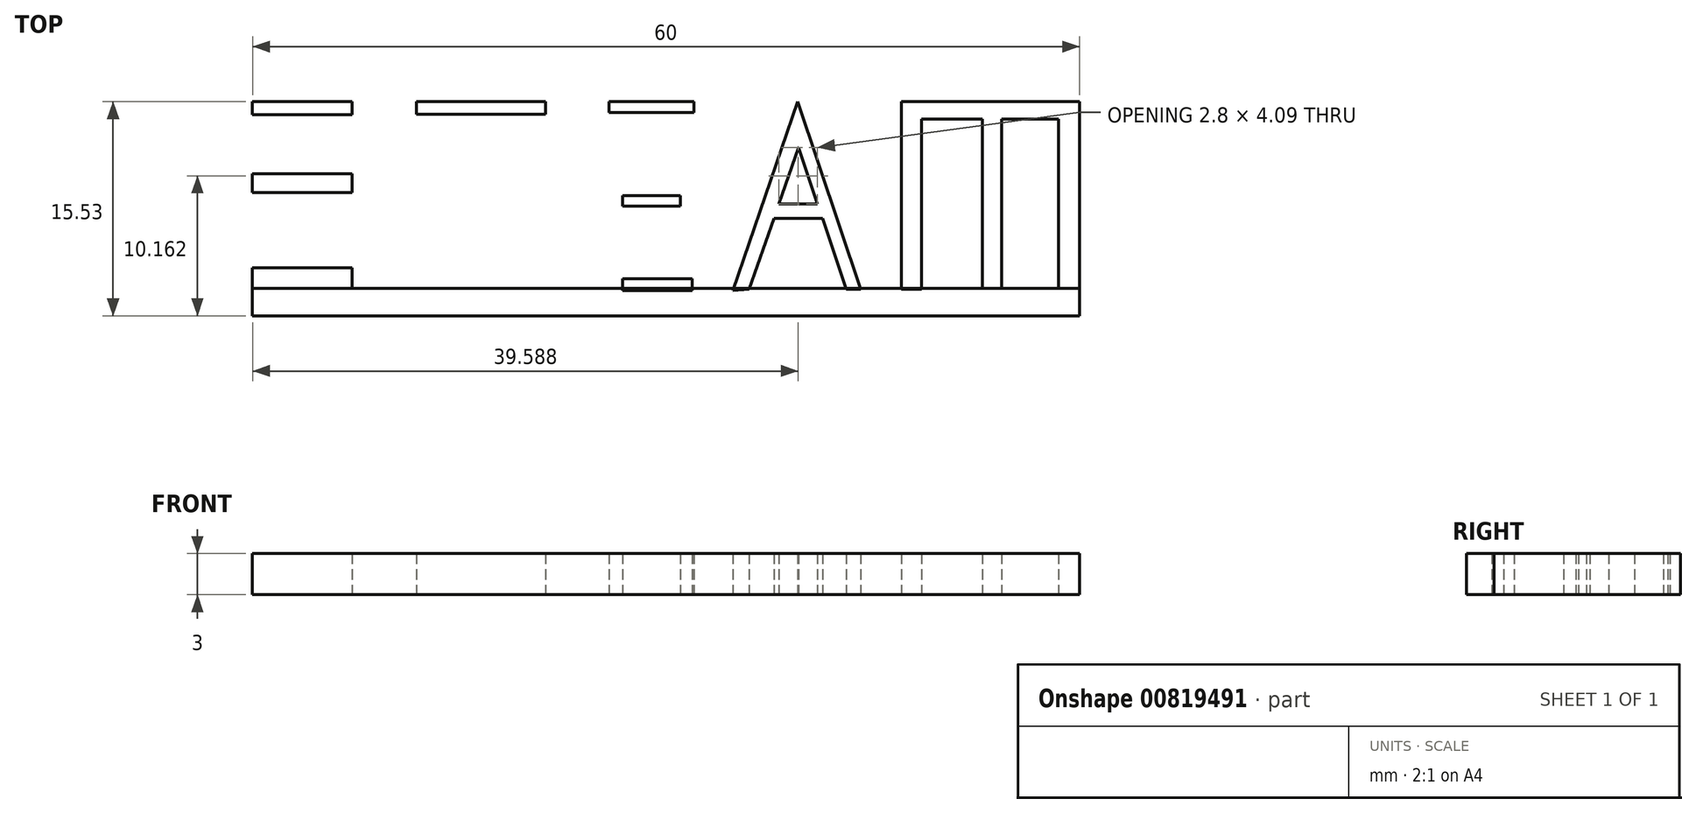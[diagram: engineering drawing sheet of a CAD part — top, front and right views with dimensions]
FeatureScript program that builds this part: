
annotation { "Feature Type Name" : "Feature", "Feature Type Description" : "" }
export const myFeature = defineFeature(function(context is Context, id is Id, definition is map)
    precondition{}
    {
        {
            var Q0;
            Q0=qCreatedBy(makeId("Top.planeOp"),FACE);
            var sketch = newSketch(context, id + "F0", { "sketchPlane" : qUnion([Q0])});
            skLineSegment(sketch, "E0.bottom", {"start": v(-31.37, 0) * mm, "end": v(-24.14, 0) * mm});
            skLineSegment(sketch, "E0.top", {"start": v(-31.37, -0.93) * mm, "end": v(-24.14, -0.93) * mm});
            skLineSegment(sketch, "E0.left", {"start": v(-31.37, 0) * mm, "end": v(-31.37, -0.93) * mm});
            skLineSegment(sketch, "E0.right", {"start": v(-24.14, 0) * mm, "end": v(-24.14, -0.93) * mm});
            skLineSegment(sketch, "E1.bottom", {"start": v(-31.37, -0.93) * mm, "end": v(-30.2, -0.93) * mm});
            skLineSegment(sketch, "E1.top", {"start": v(-31.37, -5.23) * mm, "end": v(-30.2, -5.23) * mm});
            skLineSegment(sketch, "E1.left", {"start": v(-31.37, -0.93) * mm, "end": v(-31.37, -5.23) * mm});
            skLineSegment(sketch, "E1.right", {"start": v(-30.2, -0.93) * mm, "end": v(-30.2, -5.23) * mm});
            skLineSegment(sketch, "E2.bottom", {"start": v(-31.37, -5.23) * mm, "end": v(-24.14, -5.23) * mm});
            skLineSegment(sketch, "E2.top", {"start": v(-31.37, -6.6) * mm, "end": v(-24.14, -6.6) * mm});
            skLineSegment(sketch, "E2.left", {"start": v(-31.37, -5.23) * mm, "end": v(-31.37, -6.6) * mm});
            skLineSegment(sketch, "E2.right", {"start": v(-24.14, -5.23) * mm, "end": v(-24.14, -6.6) * mm});
            skLineSegment(sketch, "E3.bottom", {"start": v(-24.14, -6.6) * mm, "end": v(-25.51, -6.6) * mm});
            skLineSegment(sketch, "E3.top", {"start": v(-24.14, -12.07) * mm, "end": v(-25.51, -12.07) * mm});
            skLineSegment(sketch, "E3.left", {"start": v(-24.14, -6.6) * mm, "end": v(-24.14, -12.07) * mm});
            skLineSegment(sketch, "E3.right", {"start": v(-25.51, -6.6) * mm, "end": v(-25.51, -12.07) * mm});
            skLineSegment(sketch, "E4.bottom", {"start": v(-24.14, -12.07) * mm, "end": v(-31.37, -12.07) * mm});
            skLineSegment(sketch, "E4.top", {"start": v(-24.14, -13.53) * mm, "end": v(-31.37, -13.53) * mm});
            skLineSegment(sketch, "E4.left", {"start": v(-24.14, -12.07) * mm, "end": v(-24.14, -13.53) * mm});
            skLineSegment(sketch, "E4.right", {"start": v(-31.37, -12.07) * mm, "end": v(-31.37, -13.53) * mm});
            skSolve(sketch);
        }
        {
            var Q0;
            Q0=qCreatedBy(makeId("Top.planeOp"),FACE);
            var sketch = newSketch(context, id + "F1", { "sketchPlane" : qUnion([Q0])});
            skLineSegment(sketch, "E5.bottom", {"start": v(-19.47, 0) * mm, "end": v(-10.1, 0) * mm});
            skLineSegment(sketch, "E5.top", {"start": v(-19.47, -0.92) * mm, "end": v(-10.1, -0.92) * mm});
            skLineSegment(sketch, "E5.left", {"start": v(-19.47, 0) * mm, "end": v(-19.47, -0.92) * mm});
            skLineSegment(sketch, "E5.right", {"start": v(-10.1, 0) * mm, "end": v(-10.1, -0.92) * mm});
            skLineSegment(sketch, "E6.bottom", {"start": v(-15.61, -0.92) * mm, "end": v(-14.26, -0.92) * mm});
            skLineSegment(sketch, "E6.top", {"start": v(-15.61, -13.7) * mm, "end": v(-14.26, -13.7) * mm});
            skLineSegment(sketch, "E6.left", {"start": v(-15.61, -0.92) * mm, "end": v(-15.61, -13.7) * mm});
            skLineSegment(sketch, "E6.right", {"start": v(-14.26, -0.92) * mm, "end": v(-14.26, -13.7) * mm});
            skSolve(sketch);
        }
        {
            var Q0;
            Q0=qCreatedBy(makeId("Top.planeOp"),FACE);
            var sketch = newSketch(context, id + "F2", { "sketchPlane" : qUnion([Q0])});
            skLineSegment(sketch, "E7.bottom", {"start": v(0.65, 0) * mm, "end": v(-5.5, 0) * mm});
            skLineSegment(sketch, "E7.top", {"start": v(0.65, -0.77) * mm, "end": v(-5.5, -0.77) * mm});
            skLineSegment(sketch, "E7.left", {"start": v(0.65, 0) * mm, "end": v(0.65, -0.77) * mm});
            skLineSegment(sketch, "E7.right", {"start": v(-5.5, 0) * mm, "end": v(-5.5, -0.77) * mm});
            skLineSegment(sketch, "E8.bottom", {"start": v(-5.5, -0.77) * mm, "end": v(-4.52, -0.77) * mm});
            skLineSegment(sketch, "E8.top", {"start": v(-5.5, -13.75) * mm, "end": v(-4.52, -13.75) * mm});
            skLineSegment(sketch, "E8.left", {"start": v(-5.5, -0.77) * mm, "end": v(-5.5, -13.75) * mm});
            skLineSegment(sketch, "E8.right", {"start": v(-4.52, -0.77) * mm, "end": v(-4.52, -13.75) * mm});
            skSolve(sketch);
        }
        {
            var Q0;
            Q0=qCreatedBy(makeId("Top.planeOp"),FACE);
            var sketch = newSketch(context, id + "F3", { "sketchPlane" : qUnion([Q0])});
            skLineSegment(sketch, "E9.bottom", {"start": v(-4.53, -6.82) * mm, "end": v(-0.35, -6.82) * mm});
            skLineSegment(sketch, "E9.top", {"start": v(-4.53, -7.58) * mm, "end": v(-0.35, -7.58) * mm});
            skLineSegment(sketch, "E9.left", {"start": v(-4.53, -6.82) * mm, "end": v(-4.53, -7.58) * mm});
            skLineSegment(sketch, "E9.right", {"start": v(-0.35, -6.82) * mm, "end": v(-0.35, -7.58) * mm});
            skLineSegment(sketch, "E10.bottom", {"start": v(-4.53, -13.7) * mm, "end": v(0.52, -13.7) * mm});
            skLineSegment(sketch, "E10.top", {"start": v(-4.53, -12.83) * mm, "end": v(0.52, -12.83) * mm});
            skLineSegment(sketch, "E10.left", {"start": v(-4.53, -13.7) * mm, "end": v(-4.53, -12.83) * mm});
            skLineSegment(sketch, "E10.right", {"start": v(0.52, -13.7) * mm, "end": v(0.52, -12.83) * mm});
            skSolve(sketch);
        }
        {
            var Q0;
            Q0=qCreatedBy(makeId("Top.planeOp"),FACE);
            var sketch = newSketch(context, id + "F4", { "sketchPlane" : qUnion([Q0])});
            skLineSegment(sketch, "E11", {"start": v(3.47, -13.69) * mm, "end": v(8.17, 0) * mm});
            skLineSegment(sketch, "E12", {"start": v(8.17, 0) * mm, "end": v(12.73, -13.62) * mm});
            skLineSegment(sketch, "E13", {"start": v(12.73, -13.62) * mm, "end": v(11.7, -13.62) * mm});
            skLineSegment(sketch, "E14", {"start": v(11.7, -13.62) * mm, "end": v(8.25, -3.32) * mm});
            skLineSegment(sketch, "E15", {"start": v(8.25, -3.32) * mm, "end": v(4.65, -13.62) * mm});
            skLineSegment(sketch, "E16", {"start": v(4.65, -13.62) * mm, "end": v(3.47, -13.69) * mm});
            skLineSegment(sketch, "E17", {"start": v(6.82, -7.41) * mm, "end": v(9.62, -7.41) * mm});
            skLineSegment(sketch, "E18", {"start": v(9.62, -7.41) * mm, "end": v(9.97, -8.47) * mm});
            skLineSegment(sketch, "E19", {"start": v(9.97, -8.47) * mm, "end": v(6.45, -8.47) * mm});
            skLineSegment(sketch, "E20", {"start": v(6.45, -8.47) * mm, "end": v(6.82, -7.41) * mm});
            skSolve(sketch);
        }
        {
            var Q0;
            Q0=qCreatedBy(makeId("Top.planeOp"),FACE);
            var sketch = newSketch(context, id + "F5", { "sketchPlane" : qUnion([Q0])});
            skLineSegment(sketch, "E21.bottom", {"start": v(15.7, -13.62) * mm, "end": v(17.15, -13.62) * mm});
            skLineSegment(sketch, "E21.top", {"start": v(15.7, 0) * mm, "end": v(17.15, 0) * mm});
            skLineSegment(sketch, "E21.left", {"start": v(15.7, -13.62) * mm, "end": v(15.7, 0) * mm});
            skLineSegment(sketch, "E21.right", {"start": v(17.15, -13.62) * mm, "end": v(17.15, 0) * mm});
            skLineSegment(sketch, "E22.bottom", {"start": v(17.15, 0) * mm, "end": v(21.57, 0) * mm});
            skLineSegment(sketch, "E22.top", {"start": v(17.15, -1.25) * mm, "end": v(21.57, -1.25) * mm});
            skLineSegment(sketch, "E22.left", {"start": v(17.15, 0) * mm, "end": v(17.15, -1.25) * mm});
            skLineSegment(sketch, "E22.right", {"start": v(21.57, 0) * mm, "end": v(21.57, -1.25) * mm});
            skLineSegment(sketch, "E23.bottom", {"start": v(21.57, 0) * mm, "end": v(22.95, 0) * mm});
            skLineSegment(sketch, "E23.top", {"start": v(21.57, -13.55) * mm, "end": v(22.95, -13.55) * mm});
            skLineSegment(sketch, "E23.left", {"start": v(21.57, 0) * mm, "end": v(21.57, -13.55) * mm});
            skLineSegment(sketch, "E23.right", {"start": v(22.95, 0) * mm, "end": v(22.95, -13.55) * mm});
            skLineSegment(sketch, "E24.bottom", {"start": v(22.95, 0) * mm, "end": v(27.1, 0) * mm});
            skLineSegment(sketch, "E24.top", {"start": v(22.95, -1.25) * mm, "end": v(27.1, -1.25) * mm});
            skLineSegment(sketch, "E24.left", {"start": v(22.95, 0) * mm, "end": v(22.95, -1.25) * mm});
            skLineSegment(sketch, "E24.right", {"start": v(27.1, 0) * mm, "end": v(27.1, -1.25) * mm});
            skLineSegment(sketch, "E25.bottom", {"start": v(27.1, 0) * mm, "end": v(28.62, 0) * mm});
            skLineSegment(sketch, "E25.top", {"start": v(27.1, -13.55) * mm, "end": v(28.62, -13.55) * mm});
            skLineSegment(sketch, "E25.left", {"start": v(27.1, 0) * mm, "end": v(27.1, -13.55) * mm});
            skLineSegment(sketch, "E25.right", {"start": v(28.62, 0) * mm, "end": v(28.62, -13.55) * mm});
            skSolve(sketch);
        }
        {
            var Q0;
            Q0=makeQuery(id+"F0.imprint","IMPRINT",FACE,{"disambiguationData":[TD([[makeQuery(id+"F0.imprint","IMPRINT",EDGE,{"derivedFrom":sQuery(id+"F0.wireOp",EDGE,"E0.bottom")}),-1.0]])]});
            var Q1;
            Q1=makeQuery(id+"F0.imprint","IMPRINT",FACE,{"disambiguationData":[TD([[makeQuery(id+"F0.imprint","IMPRINT",EDGE,{"derivedFrom":sQuery(id+"F0.wireOp",EDGE,"E1.bottom")}),-1.0]])]});
            var Q2;
            Q2=makeQuery(id+"F0.imprint","IMPRINT",FACE,{"disambiguationData":[TD([[makeQuery(id+"F0.imprint","IMPRINT",EDGE,{"derivedFrom":sQuery(id+"F0.wireOp",EDGE,"E2.top")}),1.0]])]});
            var Q3;
            Q3=makeQuery(id+"F0.imprint","IMPRINT",FACE,{"disambiguationData":[TD([[makeQuery(id+"F0.imprint","IMPRINT",EDGE,{"derivedFrom":sQuery(id+"F0.wireOp",EDGE,"E3.bottom")}),1.0]])]});
            var Q4;
            Q4=makeQuery(id+"F0.imprint","IMPRINT",FACE,{"disambiguationData":[TD([[makeQuery(id+"F0.imprint","IMPRINT",EDGE,{"derivedFrom":sQuery(id+"F0.wireOp",EDGE,"E4.top")}),-1.0]])]});
            var Q5;
            Q5=makeQuery(id+"F1.imprint","IMPRINT",FACE,{"disambiguationData":[TD([[makeQuery(id+"F1.imprint","IMPRINT",EDGE,{"derivedFrom":sQuery(id+"F1.wireOp",EDGE,"E6.bottom")}),-1.0]])]});
            var Q6;
            Q6=makeQuery(id+"F1.imprint","IMPRINT",FACE,{"disambiguationData":[TD([[makeQuery(id+"F1.imprint","IMPRINT",EDGE,{"derivedFrom":sQuery(id+"F1.wireOp",EDGE,"E5.bottom")}),-1.0]])]});
            var Q7;
            Q7=makeQuery(id+"F2.imprint","IMPRINT",FACE,{"disambiguationData":[TD([[makeQuery(id+"F2.imprint","IMPRINT",EDGE,{"derivedFrom":sQuery(id+"F2.wireOp",EDGE,"E7.bottom")}),1.0]])]});
            var Q8;
            Q8=makeQuery(id+"F2.imprint","IMPRINT",FACE,{"disambiguationData":[TD([[makeQuery(id+"F2.imprint","IMPRINT",EDGE,{"derivedFrom":sQuery(id+"F2.wireOp",EDGE,"E8.bottom")}),-1.0]])]});
            var Q9;
            Q9=makeQuery(id+"F3.imprint","IMPRINT",FACE,{"disambiguationData":[TD([[makeQuery(id+"F3.imprint","IMPRINT",EDGE,{"derivedFrom":sQuery(id+"F3.wireOp",EDGE,"E9.bottom")}),-1.0]])]});
            var Q10;
            Q10=makeQuery(id+"F3.imprint","IMPRINT",FACE,{"disambiguationData":[TD([[makeQuery(id+"F3.imprint","IMPRINT",EDGE,{"derivedFrom":sQuery(id+"F3.wireOp",EDGE,"E10.bottom")}),1.0]])]});
            var Q11;
            Q11=makeQuery(id+"F4.imprint","IMPRINT",FACE,{"disambiguationData":[TD([[makeQuery(id+"F4.imprint","IMPRINT",EDGE,{"derivedFrom":sQuery(id+"F4.wireOp",EDGE,"E11")}),-1.0]])]});
            var Q12;
            Q12=makeQuery(id+"F4.imprint","IMPRINT",FACE,{"disambiguationData":[TD([[makeQuery(id+"F4.imprint","IMPRINT",EDGE,{"derivedFrom":sQuery(id+"F4.wireOp",EDGE,"E17")}),-1.0]])]});
            var Q13;
            Q13=makeQuery(id+"F5.imprint","IMPRINT",FACE,{"disambiguationData":[TD([[makeQuery(id+"F5.imprint","IMPRINT",EDGE,{"derivedFrom":sQuery(id+"F5.wireOp",EDGE,"E21.bottom")}),1.0]])]});
            var Q14;
            {var subQ0=sQuery(id+"F5.wireOp",EDGE,"E22.bottom");Q14=makeQuery(id+"F5.imprint","IMPRINT",FACE,{"disambiguationData":[TD([[makeQuery(id+"F5.imprint","IMPRINT",EDGE,{"derivedFrom":subQ0}),-1.0]])]});}
            var Q15;
            {var subQ0=sQuery(id+"F5.wireOp",EDGE,"E24.bottom");Q15=makeQuery(id+"F5.imprint","IMPRINT",FACE,{"disambiguationData":[TD([[makeQuery(id+"F5.imprint","IMPRINT",EDGE,{"derivedFrom":subQ0}),-1.0]])]});}
            var Q16;
            {var subQ3=sQuery(id+"F5.wireOp",EDGE,"E25.bottom");Q16=makeQuery(id+"F5.imprint","IMPRINT",FACE,{"disambiguationData":[TD([[makeQuery(id+"F5.imprint","IMPRINT",EDGE,{"derivedFrom":subQ3}),-1.0]])]});}
            var Q17;
            {var subQ3=sQuery(id+"F5.wireOp",EDGE,"E23.bottom");Q17=makeQuery(id+"F5.imprint","IMPRINT",FACE,{"disambiguationData":[TD([[makeQuery(id+"F5.imprint","IMPRINT",EDGE,{"derivedFrom":subQ3}),-1.0]])]});}
            extrude(context, id + "F6", {"entities" : qUnion([Q0, Q1, Q2, Q3, Q4, Q5, Q6, Q7, Q8, Q9, Q10, Q11, Q12, Q13, Q14, Q15, Q16, Q17]), "depth" : 3 * mm, "offsetDistance" : 25 * mm});
        }
        {
            var Q0;
            Q0=makeQuery(id+"F6.opExtrude","SWEPT_FACE",FACE,{"disambiguationData":[OSD([sQuery(id+"F0.wireOp",EDGE,"E4.top")])]});
            var sketch = newSketch(context, id + "F7", { "sketchPlane" : qUnion([Q0])});
            skLineSegment(sketch, "E26.bottom", {"start": v(-31.37, 0) * mm, "end": v(28.63, 0) * mm});
            skLineSegment(sketch, "E26.top", {"start": v(-31.37, 3) * mm, "end": v(28.63, 3) * mm});
            skLineSegment(sketch, "E26.left", {"start": v(-31.37, 0) * mm, "end": v(-31.37, 3) * mm});
            skLineSegment(sketch, "E26.right", {"start": v(28.63, 0) * mm, "end": v(28.63, 3) * mm});
            skSolve(sketch);
        }
        {
            var Q0;
            {var subQ2=sQuery(id+"F7.wireOp",EDGE,"E26.right");Q0=makeQuery(id+"F7.imprint","IMPRINT",FACE,{"disambiguationData":[TD([[makeQuery(id+"F7.imprint","IMPRINT",EDGE,{"derivedFrom":subQ2}),1.0]])]});}
            var Q1;
            {var subQ2=sQuery(id+"F7.wireOp",EDGE,"E26.left");Q1=makeQuery(id+"F7.imprint","IMPRINT",FACE,{"disambiguationData":[TD([[makeQuery(id+"F7.imprint","IMPRINT",EDGE,{"derivedFrom":subQ2}),1.0]])]});}
            extrude(context, id + "F8", {"entities" : qUnion([Q0, Q1]), "depth" : 2 * mm, "offsetDistance" : 25 * mm});
        }
    });
